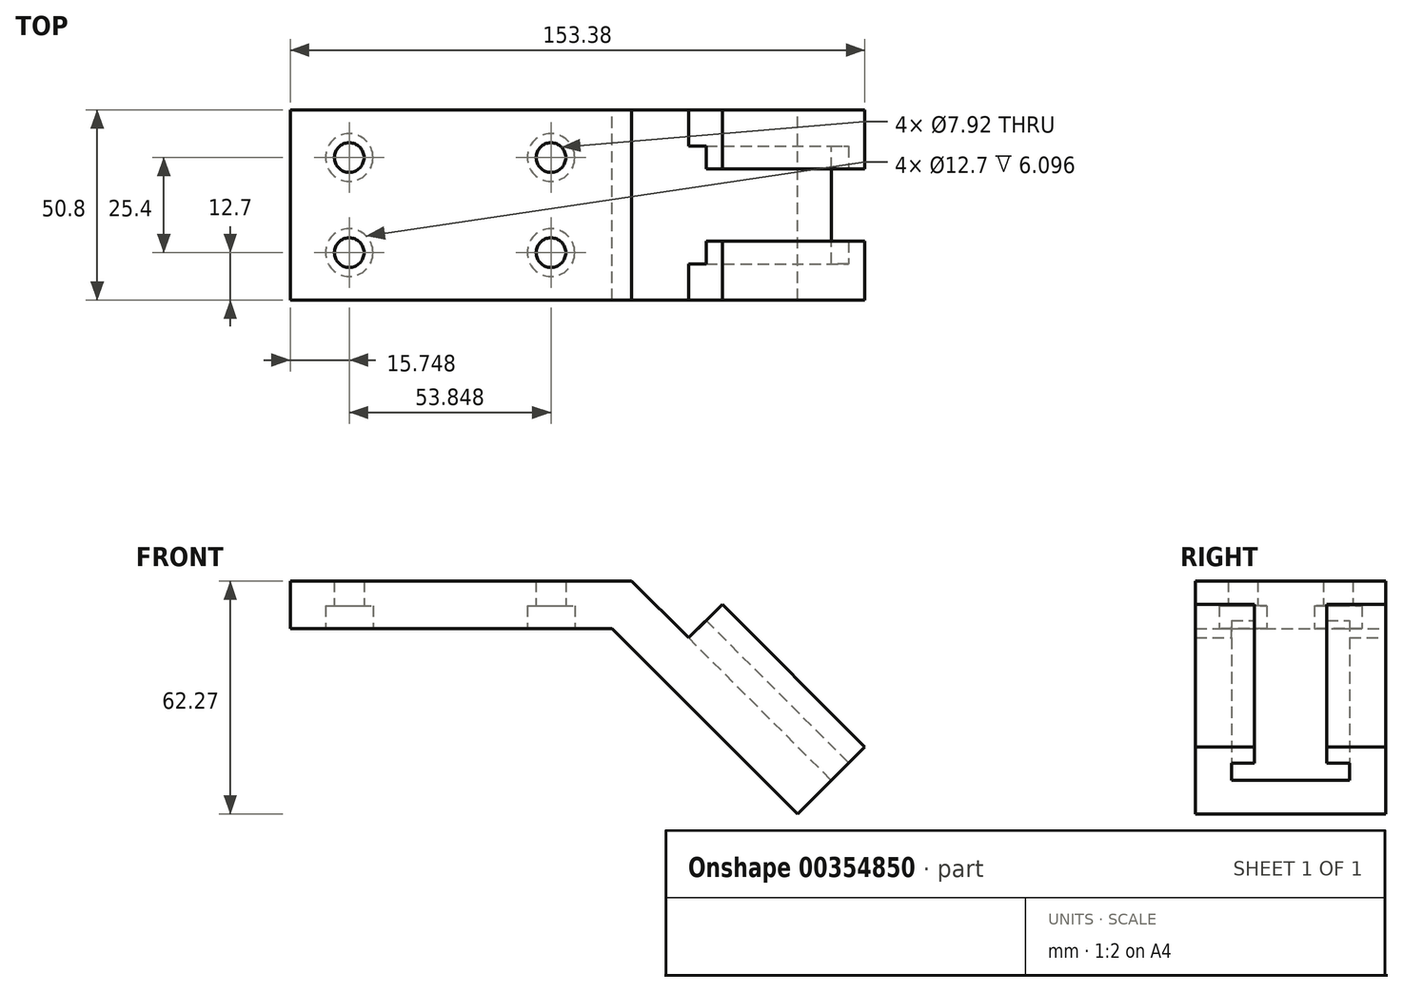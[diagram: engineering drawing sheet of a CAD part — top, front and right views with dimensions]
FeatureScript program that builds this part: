
annotation { "Feature Type Name" : "Feature", "Feature Type Description" : "" }
export const myFeature = defineFeature(function(context is Context, id is Id, definition is map)
    precondition{}
    {
        {
            var Q0;
            Q0=qCreatedBy(makeId("Front.planeOp"),FACE);
            var sketch = newSketch(context, id + "F0", { "sketchPlane" : qUnion([Q0])});
            skLineSegment(sketch, "E0", {"start": v(0, 0) * mm, "end": v(0, 12.7) * mm});
            skLineSegment(sketch, "E1", {"start": v(0, 0) * mm, "end": v(85.85, 0) * mm});
            skLineSegment(sketch, "E2", {"start": v(85.85, 0) * mm, "end": v(135.42, -49.57) * mm});
            skLineSegment(sketch, "E3", {"start": v(135.42, -49.57) * mm, "end": v(153.38, -31.61) * mm});
            skLineSegment(sketch, "E4", {"start": v(0, 12.7) * mm, "end": v(91.11, 12.7) * mm});
            skLineSegment(sketch, "E5", {"start": v(91.11, 12.7) * mm, "end": v(106.33, -2.51) * mm});
            skLineSegment(sketch, "E6", {"start": v(106.33, -2.51) * mm, "end": v(115.3, 6.47) * mm});
            skLineSegment(sketch, "E7", {"start": v(115.3, 6.47) * mm, "end": v(153.38, -31.61) * mm});
            skSolve(sketch);
        }
        {
            var Q0;
            Q0=makeQuery(id+"F0.imprint","IMPRINT",FACE,{"disambiguationData":[TD([[makeQuery(id+"F0.imprint","IMPRINT",EDGE,{"derivedFrom":sQuery(id+"F0.wireOp",EDGE,"E0")}),-1.0]])]});
            extrude(context, id + "F1", {"entities" : qUnion([Q0]), "depth" : 50.8 * mm, "symmetric" : true});
        }
        {
            var Q0;
            Q0=makeQuery(id+"F1.opExtrude","SWEPT_FACE",FACE,{"disambiguationData":[OSD([sQuery(id+"F0.wireOp",EDGE,"E4")])]});
            var sketch = newSketch(context, id + "F2", { "sketchPlane" : qUnion([Q0])});
            skCircle(sketch, "E8", {"center": v(15.75, -12.7) * mm, "radius": 3.96 * mm});
            skCircle(sketch, "E9.MirrorC", {"center": v(15.75, 12.7) * mm, "radius": 3.96 * mm});
            skLineSegment(sketch, "E10", {"start": v(15.75, -12.7) * mm, "end": v(69.6, -12.7) * mm, "construction": true});
            skCircle(sketch, "E11", {"center": v(69.6, -12.7) * mm, "radius": 3.96 * mm});
            skCircle(sketch, "E12.MirrorC", {"center": v(69.6, 12.7) * mm, "radius": 3.96 * mm});
            skSolve(sketch);
        }
        {
            var Q0;
            Q0=makeQuery(id+"F1.opExtrude","SWEPT_FACE",FACE,{"disambiguationData":[OSD([sQuery(id+"F0.wireOp",EDGE,"E1")])]});
            var sketch = newSketch(context, id + "F3", { "sketchPlane" : qUnion([Q0])});
            skPoint(sketch, "E13.0", {"position": v(15.75, -12.7) * mm});
            skPoint(sketch, "E13.1", {"position": v(15.75, 12.7) * mm});
            skPoint(sketch, "E13.2", {"position": v(69.6, 12.7) * mm});
            skPoint(sketch, "E13.3", {"position": v(69.6, -12.7) * mm});
            skSolve(sketch);
        }
        {
            var Q0;
            Q0=sQuery(id+"F3.wireOp",VERTEX,"E13.1");
            var Q1;
            Q1=sQuery(id+"F3.wireOp",VERTEX,"E13.0");
            var Q2;
            Q2=sQuery(id+"F3.wireOp",VERTEX,"E13.2");
            var Q3;
            Q3=sQuery(id+"F3.wireOp",VERTEX,"E13.3");
            var Q4;
            Q4=makeQuery(id+"F1.opExtrude","SWEPT_BODY",BODY,{"disambiguationData":[OSD([sQuery(id+"F0.wireOp",EDGE,"E0"),sQuery(id+"F0.wireOp",EDGE,"E1"),sQuery(id+"F0.wireOp",EDGE,"E2"),sQuery(id+"F0.wireOp",EDGE,"E3"),sQuery(id+"F0.wireOp",EDGE,"E4"),sQuery(id+"F0.wireOp",EDGE,"E5"),sQuery(id+"F0.wireOp",EDGE,"E6"),sQuery(id+"F0.wireOp",EDGE,"E7")])]});
            hole(context, id + "F4", {"style" : HoleStyle.C_BORE, "endStyle" : HoleEndStyle.THROUGH, "holeDiameter" : 7.92 * mm, "cBoreDiameter" : 12.7 * mm, "cBoreDepth" : 6.1 * mm, "isTappedThrough" : true, "tappedDepth" : 12.7 * mm, "tapClearance" : 3, "locations" : qUnion([Q0, Q1, Q2, Q3]), "scope" : qUnion([Q4])});
        }
        {
            var Q0;
            Q0=makeQuery(id+"F1.opExtrude","SWEPT_FACE",FACE,{"disambiguationData":[OSD([sQuery(id+"F0.wireOp",EDGE,"E3")])]});
            var sketch = newSketch(context, id + "F5", { "sketchPlane" : qUnion([Q0])});
            skLineSegment(sketch, "E14", {"start": v(-9.65, 86.1) * mm, "end": v(-9.65, 80.01) * mm});
            skLineSegment(sketch, "E15", {"start": v(-9.65, 80.01) * mm, "end": v(-15.75, 80.01) * mm});
            skLineSegment(sketch, "E16", {"start": v(-15.75, 80.01) * mm, "end": v(-15.75, 73.4) * mm});
            skLineSegment(sketch, "E17", {"start": v(-15.75, 73.4) * mm, "end": v(15.75, 73.4) * mm});
            skLineSegment(sketch, "E18", {"start": v(15.75, 73.4) * mm, "end": v(15.75, 80.01) * mm});
            skLineSegment(sketch, "E19", {"start": v(15.75, 80.01) * mm, "end": v(9.65, 80.01) * mm});
            skLineSegment(sketch, "E20", {"start": v(9.65, 80.01) * mm, "end": v(9.65, 86.1) * mm});
            skSolve(sketch);
        }
        {
            var Q0;
            {var subQ0=sQuery(id+"F5.wireOp",EDGE,"E14");Q0=makeQuery(id+"F5.imprint","IMPRINT",FACE,{"disambiguationData":[TD([[makeQuery(id+"F5.imprint","IMPRINT",EDGE,{"derivedFrom":subQ0}),1.0]])]});}
            extrude(context, id + "F6", {"entities" : qUnion([Q0]), "operationType" : NewBodyOperationType.REMOVE, "endBound" : BoundingType.THROUGH_ALL, "oppositeDirection" : true, "depth" : 25.4 * mm});
        }
        {
            var Q0;
            {var subQ0=sQuery(id+"F0.wireOp",EDGE,"E7");Q0=makeQuery(id+"F6.boolean.opBoolean","SPLIT",FACE,{"disambiguationData":[TD([makeQuery(id+"F6.opExtrude","SWEPT_FACE",FACE,{"disambiguationData":[OSD([sQuery(id+"F5.wireOp",EDGE,"E20")])]})])],"derivedFrom":makeQuery(id+"F1.opExtrude","SWEPT_FACE",FACE,{"disambiguationData":[OSD([subQ0])]})});}
            var sketch = newSketch(context, id + "F7", { "sketchPlane" : qUnion([Q0])});
            skLineSegment(sketch, "E21.0", {"start": v(76.96, -25.4) * mm, "end": v(130.81, -25.4) * mm});
            skLineSegment(sketch, "E21.1", {"start": v(76.96, -9.65) * mm, "end": v(130.81, -9.65) * mm});
            skLineSegment(sketch, "E21.2", {"start": v(130.81, -25.4) * mm, "end": v(130.81, -9.65) * mm});
            skLineSegment(sketch, "E21.3", {"start": v(130.81, 9.65) * mm, "end": v(130.81, 25.4) * mm});
            skLineSegment(sketch, "E21.4", {"start": v(130.81, -15.75) * mm, "end": v(130.81, 15.75) * mm});
            skLineSegment(sketch, "E21.5", {"start": v(76.96, 25.4) * mm, "end": v(130.81, 25.4) * mm});
            skLineSegment(sketch, "E21.6", {"start": v(76.96, 9.65) * mm, "end": v(130.81, 9.65) * mm});
            skArc(sketch, "E22", {"start": v(124.44, -25.4) * mm, "mid": v(130.81, 0) * mm, "end": v(124.44, 25.4) * mm});
            skLineSegment(sketch, "E23", {"start": v(76.96, 9.65) * mm, "end": v(76.96, -9.65) * mm, "construction": true});
            skSolve(sketch);
        }
        {
            var Q0;
            {var subQ3=sQuery(id+"F7.wireOp",EDGE,"E21.2");Q0=makeQuery(id+"F7.imprint","IMPRINT",FACE,{"disambiguationData":[TD([[makeQuery(id+"F7.imprint","IMPRINT",EDGE,{"derivedFrom":subQ3}),1.0]])]});}
            var Q1;
            {var subQ6=sQuery(id+"F7.wireOp",EDGE,"E21.3");Q1=makeQuery(id+"F7.imprint","IMPRINT",FACE,{"disambiguationData":[TD([[makeQuery(id+"F7.imprint","IMPRINT",EDGE,{"derivedFrom":subQ6}),1.0]])]});}
            var Q2;
            {var subQ0=sQuery(id+"F7.wireOp",EDGE,"E21.4");var subQ1=sQuery(id+"F7.wireOp",EDGE,"E21.1");var subQ2=makeQuery(id+"F7.imprint","INTERSECT",VERTEX,{"derivedFrom":[subQ1,subQ0]});Q2=makeQuery(id+"F7.imprint","IMPRINT",FACE,{"disambiguationData":[TD([[makeQuery(id+"F7.imprint","IMPRINT",EDGE,{"disambiguationData":[TD([[subQ2,1.0]])],"derivedFrom":subQ1}),1.0]])]});}
            var Q3;
            {var subQ0=sQuery(id+"F7.wireOp",EDGE,"E21.6");var subQ1=sQuery(id+"F7.wireOp",EDGE,"E21.4");var subQ2=makeQuery(id+"F7.imprint","INTERSECT",VERTEX,{"derivedFrom":[subQ1,subQ0]});Q3=makeQuery(id+"F7.imprint","IMPRINT",FACE,{"disambiguationData":[TD([[makeQuery(id+"F7.imprint","IMPRINT",EDGE,{"disambiguationData":[TD([[subQ2,1.0]])],"derivedFrom":subQ1}),1.0]])]});}
            extrude(context, id + "F8", {"entities" : qUnion([Q0, Q1, Q2, Q3]), "operationType" : NewBodyOperationType.REMOVE, "endBound" : BoundingType.THROUGH_ALL, "oppositeDirection" : true, "depth" : 25.4 * mm});
        }
    });
